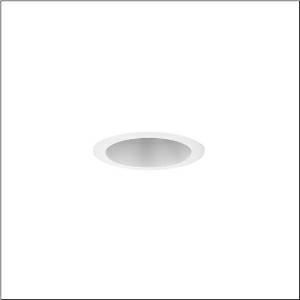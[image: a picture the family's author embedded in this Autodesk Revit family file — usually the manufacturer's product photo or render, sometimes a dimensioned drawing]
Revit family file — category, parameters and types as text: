
# Revit family: lunis_31_mini_51dn16de31
name_source: partatom
category: Lighting Fixtures
units: mm (PartAtom-declared; Revit-internal decimal feet)

## family parameters
Cut with Voids When Loaded = No
Host = Face
Light Source = No
Part Type = Normal
Room Calculation Point = No
Round Connector Dimension = Use Diameter
Shared = No

## types (1)
- Lunis 31 mini (1 x LED, 1000 lm, 8.3 W, 3000K)
    Apparent Load = 8 VA
    CIE Flux Codes = 69 93 99 100 100
    Color Rendering = 80
    Color Temperature = 3000K
    Default Elevation = 1800 mm
    Description = Lunis 31,  mini, downlight, light control with reflector, light emission: direct distribution, LED rated luminous flux: 1.000lm, light colour: 830, control gear: ECG DALI, mains connection: 220..240V, AC, 50/60Hz, housing, white, protection rating (complete): IP20, insulation class (complete): insulation class II (safety insulation), certification: CE, packaging unit: 1 piece
    Height = 0 mm  [stored 0 ft]
    Lamp = 1 x LED
    Lamp Light Flux = 1000 lm
    Lamp Power = 8.3 W
    Lamp count = 1
    Length = 188 mm  [stored 0.616798 ft]
    Luminous efficacy = 120 lm/W
    Manufacturer = Siteco
    ModVariant = No
    Model = 51DN16DE31
    Mounting Place = Ceiling
    Mounting Type = Recessed
    Number of Poles = 1
    OnlyDefault = Yes
    Power Factor = 1
    Product Name = Lunis 31 mini
    Product group = downlight | ceiling recessed
    ProductGroupID = 402
    Protection Class = Protection class II
    Protection Degree = IP 20
    RLX_Detail_Level = 1
    RlxData = <blob elided: 21825 chars, md5=dfae3360>
    Socket = socket
    Standby Power = 0 W
    System Light Flux = 1000 lm
    System Power = 8 W
    Type Comments = Product without accessories
    Type Image = l_1005624.jpg
    URL = http://relux.com
    VarID = ---
    Voltage = 0 V
    Weight = 0.00 kg
    Width = 0 mm  [stored 0 ft]

note: [stored X ft] marks values corroborated as IEEE doubles in the binary element streams (Revit-internal decimal feet)

## geometry (parser evidence)
native form markers: Blend x4, Sweep x12
no freeform markers — native parametric forms only
